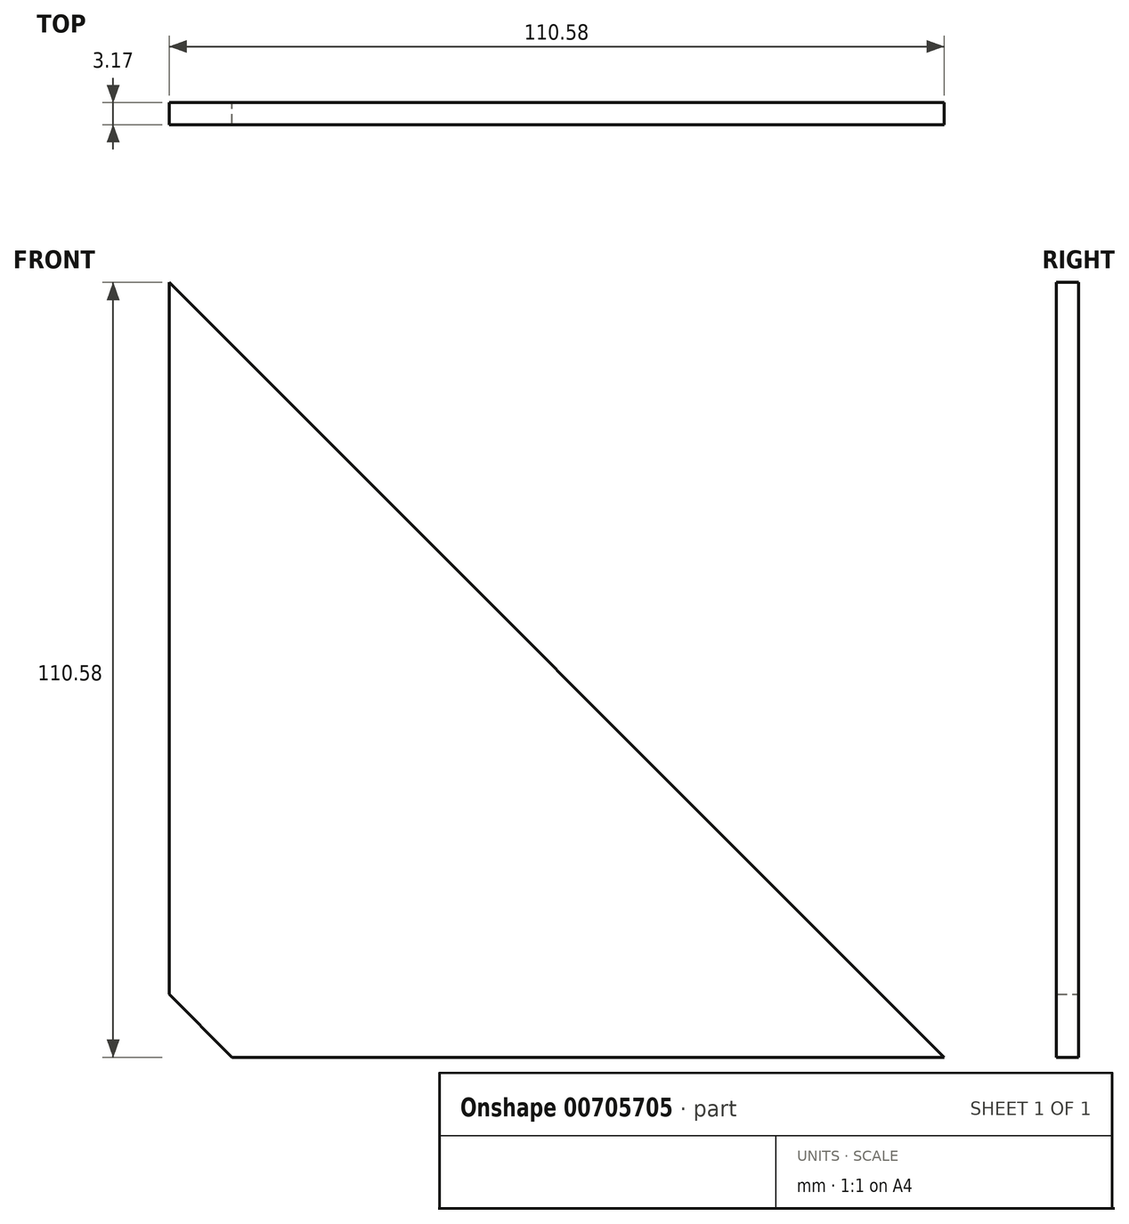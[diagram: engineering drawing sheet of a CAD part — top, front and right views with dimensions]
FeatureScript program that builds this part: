
annotation { "Feature Type Name" : "Feature", "Feature Type Description" : "" }
export const myFeature = defineFeature(function(context is Context, id is Id, definition is map)
    precondition{}
    {
        {
            var Q0;
            Q0=qCreatedBy(makeId("Front.planeOp"),FACE);
            var sketch = newSketch(context, id + "F0", { "sketchPlane" : qUnion([Q0])});
            skLineSegment(sketch, "E0", {"start": v(0, 0) * mm, "end": v(101.6, 0) * mm});
            skLineSegment(sketch, "E1", {"start": v(101.6, 0) * mm, "end": v(-8.98, 110.58) * mm});
            skLineSegment(sketch, "E2", {"start": v(-8.98, 110.58) * mm, "end": v(-8.98, 8.98) * mm});
            skLineSegment(sketch, "E3", {"start": v(-8.98, 8.98) * mm, "end": v(0, 0) * mm});
            skSolve(sketch);
        }
        {
            var Q0;
            Q0 = qSketchRegion(id + "F0", true);
            extrude(context, id + "F1", {"entities" : qUnion([Q0]), "depth" : 3.17 * mm, "offsetDistance" : 25.4 * mm});
        }
    });
